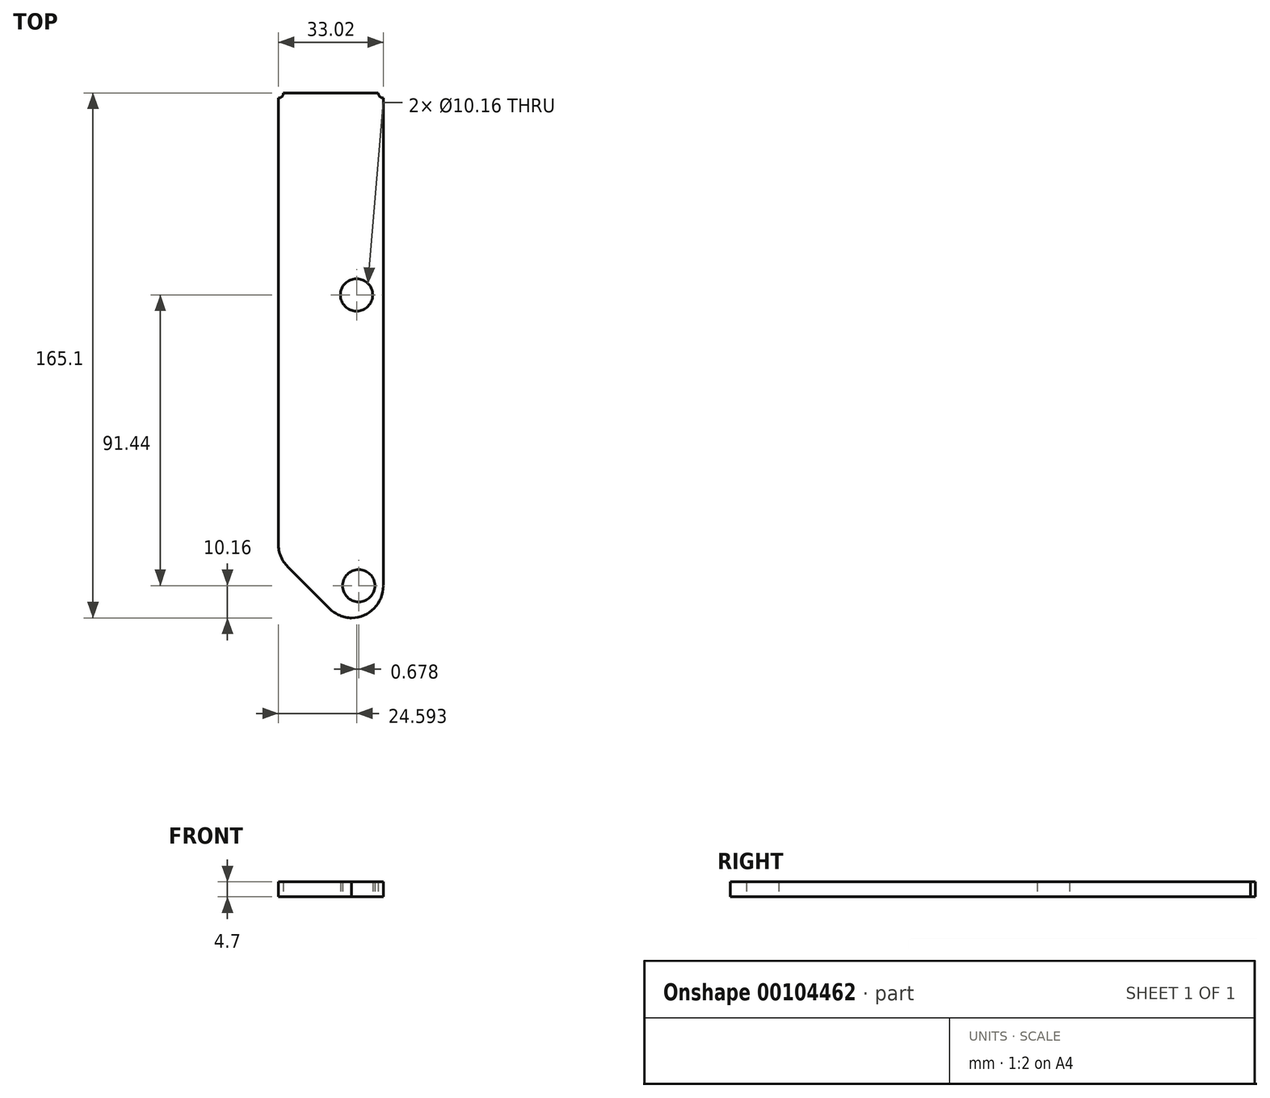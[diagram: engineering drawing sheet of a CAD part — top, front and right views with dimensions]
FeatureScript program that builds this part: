
annotation { "Feature Type Name" : "Feature", "Feature Type Description" : "" }
export const myFeature = defineFeature(function(context is Context, id is Id, definition is map)
    precondition{}
    {
        {
            var Q0;
            Q0=qCreatedBy(makeId("Top.planeOp"),FACE);
            var sketch = newSketch(context, id + "F0", { "sketchPlane" : qUnion([Q0])});
            skLineSegment(sketch, "E0", {"start": v(0, 165.1) * mm, "end": v(33.02, 165.1) * mm});
            skLineSegment(sketch, "E1", {"start": v(33.02, 165.1) * mm, "end": v(33.02, 0) * mm});
            skCircle(sketch, "E2", {"center": v(25.27, 10.16) * mm, "radius": 5.08 * mm});
            skCircle(sketch, "E3", {"center": v(24.6, 101.6) * mm, "radius": 5.08 * mm});
            skLineSegment(sketch, "E4", {"start": v(0, 19.05) * mm, "end": v(19.05, 0) * mm});
            skLineSegment(sketch, "E5", {"start": v(33.02, 0) * mm, "end": v(19.05, 0) * mm});
            skLineSegment(sketch, "E6", {"start": v(0, 19.05) * mm, "end": v(0, 165.1) * mm});
            skCircle(sketch, "E7", {"center": v(33.02, 165.1) * mm, "radius": 1.59 * mm});
            skCircle(sketch, "E8", {"center": v(0, 165.1) * mm, "radius": 1.59 * mm});
            skSolve(sketch);
        }
        {
            var Q0;
            Q0=makeQuery(id+"F0.imprint","IMPRINT",FACE,{"disambiguationData":[TD([[makeQuery(id+"F0.imprint","IMPRINT",EDGE,{"derivedFrom":sQuery(id+"F0.wireOp",EDGE,"E2")}),-1.0]])]});
            var Q1;
            {var subQ5=sQuery(id+"F0.wireOp",EDGE,"Ny4iFeSR-KQTB-Bs2D-dSeo-kTBURi5bTj4H");var subQ9=sQuery(id+"F0.wireOp",EDGE,"1NBGa66K-6Ykr-mjlE-zPSq-amoe6wd6OEds");var subQ14=makeQuery(id+"F0.imprint","INTERSECT",VERTEX,{"derivedFrom":[subQ9,subQ5]});Q1=makeQuery(id+"F0.imprint","IMPRINT",FACE,{"disambiguationData":[TD([[makeQuery(id+"F0.imprint","IMPRINT",EDGE,{"disambiguationData":[TD([[subQ14,1.0]])],"derivedFrom":subQ9}),1.0]])]});}
            var Q2;
            {var subQ5=sQuery(id+"F0.wireOp",EDGE,"1NBGa66K-6Ykr-mjlE-zPSq-amoe6wd6OEds");var subQ7=sQuery(id+"F0.wireOp",EDGE,"Ny4iFeSR-KQTB-Bs2D-dSeo-kTBURi5bTj4H");var subQ11=makeQuery(id+"F0.imprint","INTERSECT",VERTEX,{"derivedFrom":[subQ5,subQ7]});Q2=makeQuery(id+"F0.imprint","IMPRINT",FACE,{"disambiguationData":[TD([[makeQuery(id+"F0.imprint","IMPRINT",EDGE,{"disambiguationData":[TD([[subQ11,-1.0]])],"derivedFrom":subQ5}),1.0]])]});}
            var Q3;
            {var subQ8=sQuery(id+"F0.wireOp",EDGE,"E8");var subQ10=sQuery(id+"F0.wireOp",EDGE,"E0");var subQ11=makeQuery(id+"F0.imprint","INTERSECT",VERTEX,{"derivedFrom":[subQ10,subQ8]});Q3=makeQuery(id+"F0.imprint","IMPRINT",FACE,{"disambiguationData":[TD([[makeQuery(id+"F0.imprint","IMPRINT",EDGE,{"disambiguationData":[TD([[subQ11,-1.0]])],"derivedFrom":subQ10}),1.0]])]});}
            extrude(context, id + "F1", {"entities" : qUnion([Q0, Q1, Q2, Q3]), "depth" : 4.7 * mm});
        }
        {
            var Q0;
            Q0=makeQuery(id+"F1.opExtrude","SWEPT_EDGE",EDGE,{"disambiguationData":[OSD([sQuery(id+"F0.wireOp",EDGE,"E4"),sQuery(id+"F0.wireOp",EDGE,"E6")])]});
            var Q1;
            Q1=makeQuery(id+"F1.opExtrude","SWEPT_EDGE",EDGE,{"disambiguationData":[OSD([sQuery(id+"F0.wireOp",EDGE,"E4"),sQuery(id+"F0.wireOp",EDGE,"E5")])]});
            var Q2;
            Q2=makeQuery(id+"F1.opExtrude","SWEPT_EDGE",EDGE,{"disambiguationData":[OSD([sQuery(id+"F0.wireOp",EDGE,"E1"),sQuery(id+"F0.wireOp",EDGE,"E5")])]});
            fillet(context, id + "F2", {"entities" : qUnion([Q0, Q1, Q2]), "radius" : 10.16 * mm, "tangentPropagation" : true, "allowEdgeOverflow" : false});
        }
    });
